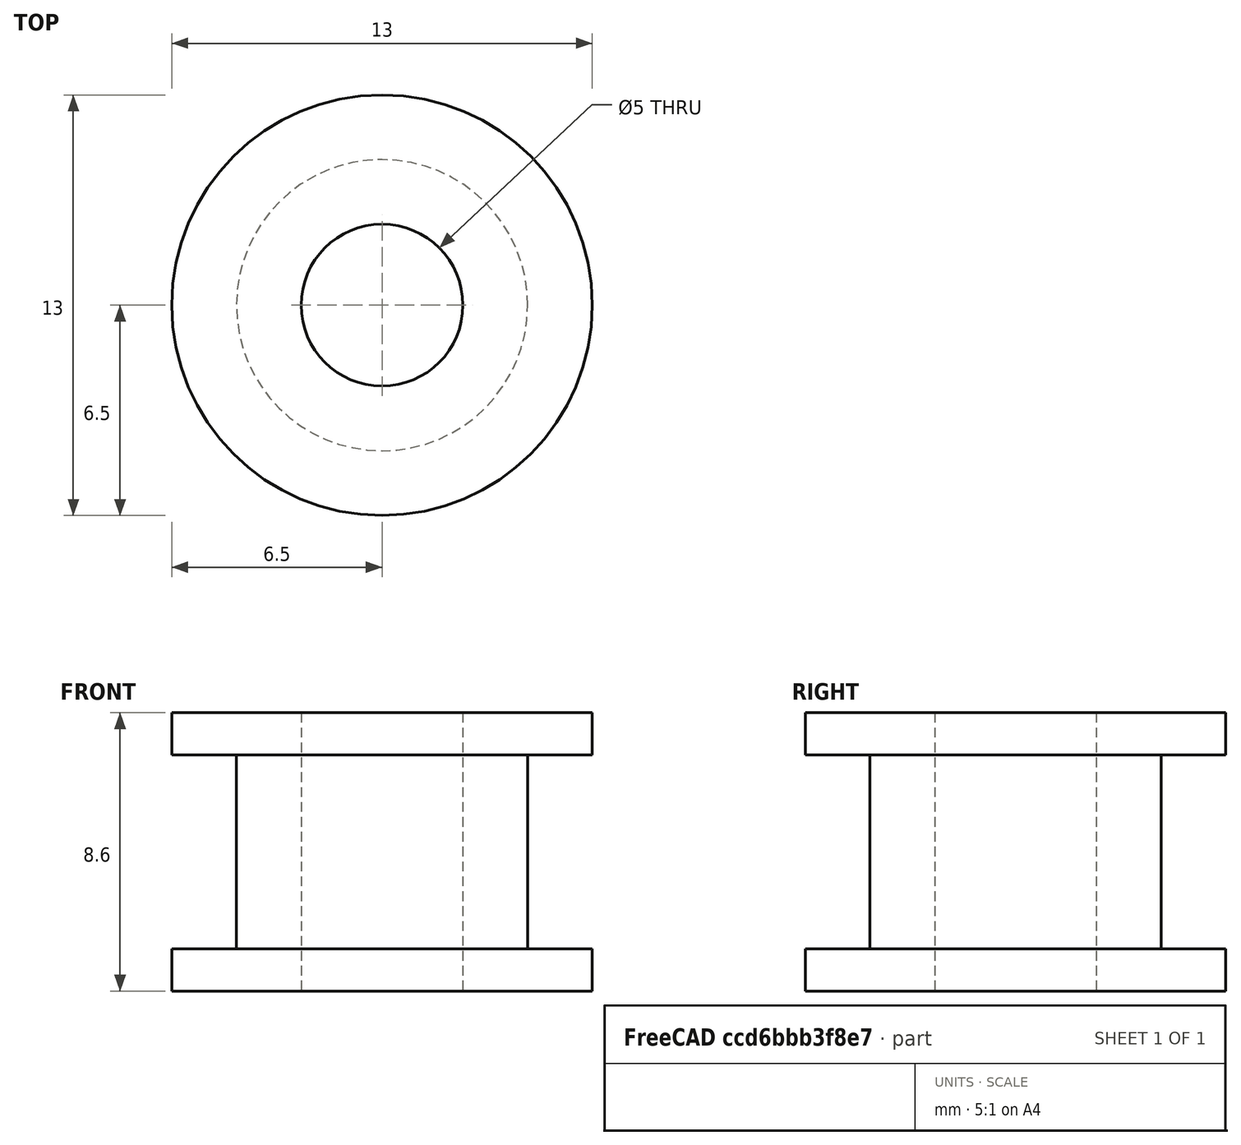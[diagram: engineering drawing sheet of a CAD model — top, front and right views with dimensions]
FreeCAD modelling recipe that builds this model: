
FCSTD DOCUMENT  (FreeCAD 0.18R)
Label: y-idler-pulley
License: All rights reserved
LicenseURL: http://en.wikipedia.org/wiki/All_rights_reserved
objects: Sketcher::SketchObject×1, PartDesign::Revolution×1, PartDesign::Body×1
note: 4 computed .brp shape members not serialized (recipe doc carries the construction recipe); baked Part::Feature solids carry a one-line shape summary decoded from their .brp

FEATURE [Sketcher::SketchObject] Sketch
  MapMode = 5
  Placement = pos=(0,0,0) rot=(0.57735,0.57735,0.57735;2.0944rad)
  Support = -> [YZ_Plane]
  sketch-geometry (8):
    g0: LineSegment StartX=-6.5 StartY=8.6 StartZ=0 EndX=-2.5 EndY=8.6 EndZ=0
    g1: LineSegment StartX=-6.5 StartY=8.6 StartZ=0 EndX=-6.5 EndY=7.3 EndZ=0
    g2: LineSegment StartX=-6.5 StartY=7.3 StartZ=0 EndX=-4.5 EndY=7.3 EndZ=0
    g3: LineSegment StartX=-4.5 StartY=7.3 StartZ=0 EndX=-4.5 EndY=1.3 EndZ=0
    g4: LineSegment StartX=-4.5 StartY=1.3 StartZ=0 EndX=-6.5 EndY=1.3 EndZ=0
    g5: LineSegment StartX=-6.5 StartY=1.3 StartZ=0 EndX=-6.5 EndY=0 EndZ=0
    g6: LineSegment StartX=-6.5 StartY=0 StartZ=0 EndX=-2.5 EndY=0 EndZ=0
    g7: LineSegment StartX=-2.5 StartY=8.6 StartZ=0 EndX=-2.5 EndY=0 EndZ=0
  constraints (24):
    c: Horizontal(g0)
    c: Horizontal(g2)
    c: Horizontal(g4)
    c: PointOnObject(g6,g-1)
    c: Coincident(g0,g1)
    c: Coincident(g2,g1)
    c: Vertical(g1)
    c: Vertical(g3)
    c: Coincident(g3,g2)
    c: Coincident(g3,g4)
    c: Coincident(g4,g5)
    c: Coincident(g5,g6)
    c: Vertical(g5)
    c: DistanceX(g0,g0) = 4
    c: DistanceY(g1,g1) = 1.3
    c: Equal(g1,g5)
    c: DistanceX(g4,g1) = 0
    c: DistanceX(g2,g2) = 2
    c: Horizontal(g6)
    c: DistanceX(g6,g-1) = 2.5
    c: DistanceX(g6,g0) = 0
    c: Coincident(g7,g0)
    c: Coincident(g7,g6)
    c: DistanceY(g3,g3) = 6
FEATURE [PartDesign::Revolution] Revolution
  Angle = 360
  Axis = (-2e-16,3e-16,1)
  Base = (0,0,0)
  Placement = pos=(0,0,0) rot=(0.57735,0.57735,0.57735;2.0944rad)
  Profile = -> Sketch
  ReferenceAxis = -> Sketch [V_Axis]
FEATURE [PartDesign::Body] Body  label="y-idler-pulley"
  Group = -> [Sketch,Revolution]
  Origin = -> Origin
  Tip = -> Revolution
